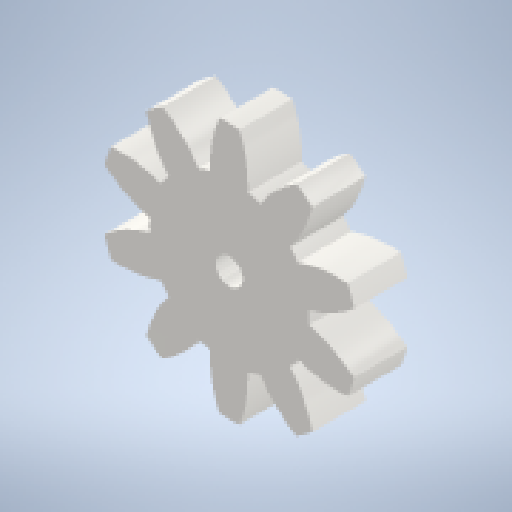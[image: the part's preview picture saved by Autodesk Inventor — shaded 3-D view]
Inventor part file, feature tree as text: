
AUTODESK INVENTOR PART (.ipt)
format: ipt  version: 2024 (Build 280153000, 153)  size: 222,208 bytes
history: native  units: mm (DEFAULTED — no unit token found)
features: plane x3, other x3, extrude x2, sketch x2
ambient origin geometry x8: Origin, YZ Plane, XZ Plane, XY Plane, X Axis, Y Axis, Z Axis, Center Point
bodies: Solid1 (feature_tree)
feature tree (10):
  extrude  "Extrusion1"  Depth=5.0mm TaperAngle=0.0deg
  plane  "Work Plane2"
  plane  "Work Plane8"
  plane  "Work Plane9"
  other  "Spur Gear"
  extrude  "Extrusion2"  Depth=10.0mm TaperAngle=0.0deg
  sketch  "Sketch1"  dims[d0=24.0mm d1=5.0mm d2=0.0mm]
  other  "Srf1"
  sketch  "Sketch3"  dims[d3=20.0mm d4=10.0mm d5=0.0mm d16=40.0mm d17=0.0mm d34=3.141593mm d39=0.0mm d41=0.0mm d43=40.0mm d46=40.0mm d47=0.0mm d48=0.0mm d49=2.5mm d50=10.0mm d51=0.0mm]
  other  "Pitch Diameter"
